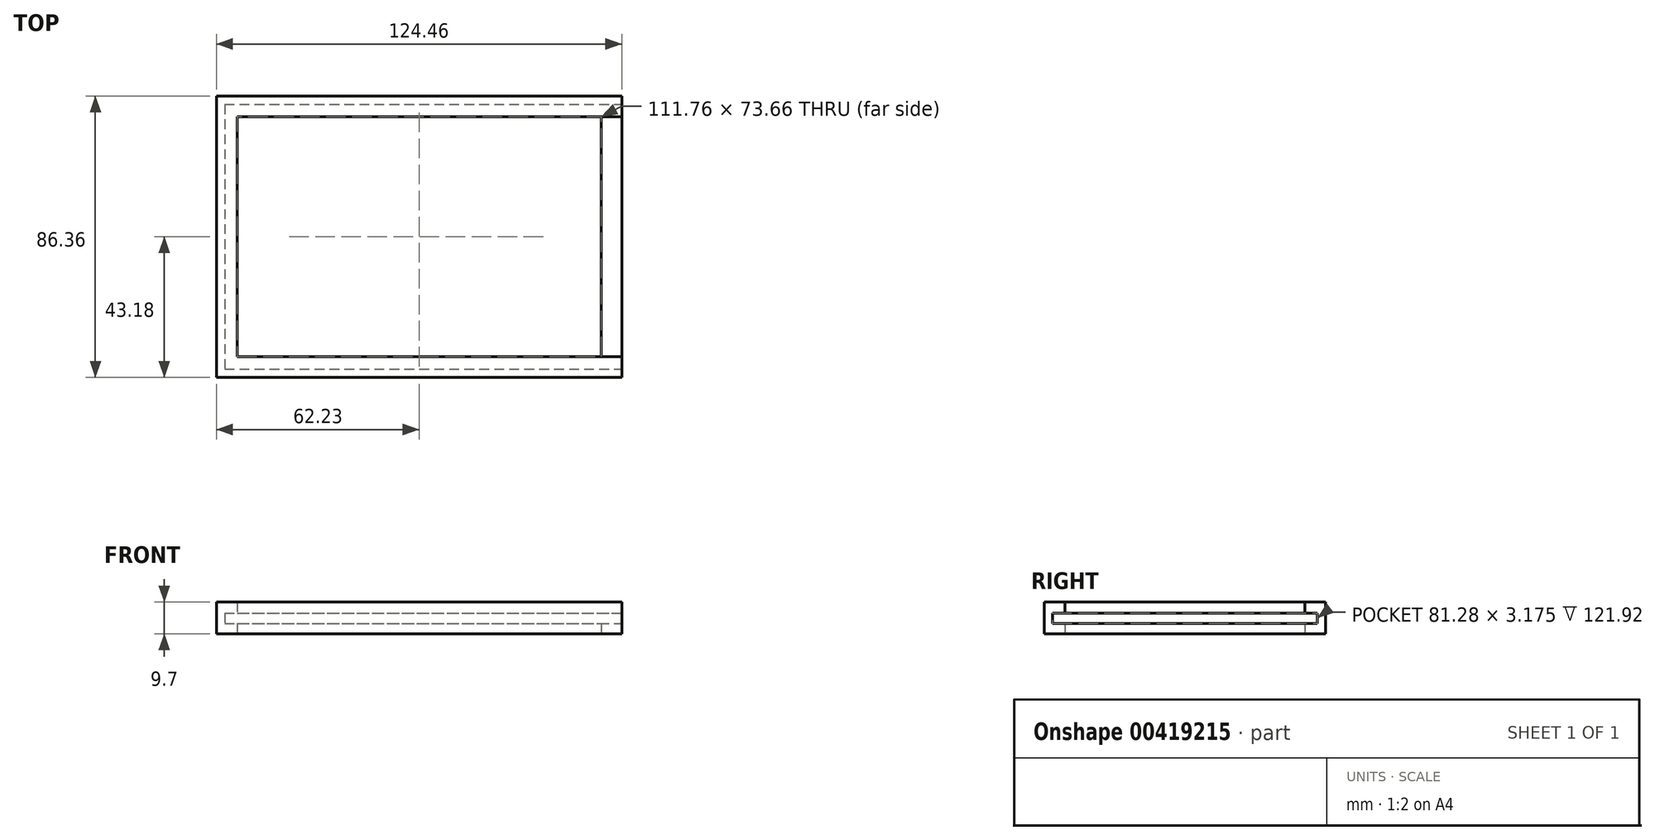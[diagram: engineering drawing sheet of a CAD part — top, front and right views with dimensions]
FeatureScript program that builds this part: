
annotation { "Feature Type Name" : "Feature", "Feature Type Description" : "" }
export const myFeature = defineFeature(function(context is Context, id is Id, definition is map)
    precondition{}
    {
        {
            var Q0;
            Q0=qCreatedBy(makeId("Top.planeOp"),FACE);
            var sketch = newSketch(context, id + "F0", { "sketchPlane" : qUnion([Q0])});
            skLineSegment(sketch, "E0.bottom", {"start": v(-55.88, 36.83) * mm, "end": v(55.88, 36.83) * mm});
            skLineSegment(sketch, "E0.top", {"start": v(-55.88, -36.83) * mm, "end": v(55.88, -36.83) * mm});
            skLineSegment(sketch, "E0.left", {"start": v(-55.88, 36.83) * mm, "end": v(-55.88, -36.83) * mm});
            skLineSegment(sketch, "E0.right", {"start": v(55.88, 36.83) * mm, "end": v(55.88, -36.83) * mm});
            skPoint(sketch, "E0.middle", {"position": v(0, 0) * mm});
            skLineSegment(sketch, "E1.bottom", {"start": v(-59.7, 40.64) * mm, "end": v(59.7, 40.64) * mm});
            skLineSegment(sketch, "E1.top", {"start": v(-59.7, -40.64) * mm, "end": v(59.7, -40.64) * mm});
            skLineSegment(sketch, "E1.left", {"start": v(-59.7, 40.64) * mm, "end": v(-59.7, -40.64) * mm});
            skLineSegment(sketch, "E1.right", {"start": v(59.7, 40.64) * mm, "end": v(59.7, -40.64) * mm});
            skLineSegment(sketch, "E2.bottom", {"start": v(-62.23, 43.18) * mm, "end": v(62.23, 43.18) * mm});
            skLineSegment(sketch, "E2.top", {"start": v(-62.23, -43.18) * mm, "end": v(62.23, -43.18) * mm});
            skLineSegment(sketch, "E2.left", {"start": v(-62.23, 43.18) * mm, "end": v(-62.23, -43.18) * mm});
            skLineSegment(sketch, "E2.right", {"start": v(62.23, 43.18) * mm, "end": v(62.23, -43.18) * mm});
            skLineSegment(sketch, "E3", {"start": v(59.7, 40.64) * mm, "end": v(62.23, 40.64) * mm});
            skLineSegment(sketch, "E4", {"start": v(55.88, 36.83) * mm, "end": v(62.23, 36.83) * mm});
            skLineSegment(sketch, "E5", {"start": v(55.88, -36.83) * mm, "end": v(62.23, -36.83) * mm});
            skLineSegment(sketch, "E6", {"start": v(59.7, -40.64) * mm, "end": v(62.23, -40.64) * mm});
            skSolve(sketch);
        }
        {
            var Q0;
            Q0=makeQuery(id+"F0.imprint","IMPRINT",FACE,{"disambiguationData":[TD([[makeQuery(id+"F0.imprint","IMPRINT",EDGE,{"derivedFrom":sQuery(id+"F0.wireOp",EDGE,"E0.bottom")}),1.0]])]});
            var Q1;
            {var subQ0=sQuery(id+"F0.wireOp",EDGE,"E3");Q1=makeQuery(id+"F0.imprint","IMPRINT",FACE,{"disambiguationData":[TD([[makeQuery(id+"F0.imprint","IMPRINT",EDGE,{"derivedFrom":subQ0}),-1.0]])]});}
            var Q2;
            {var subQ0=sQuery(id+"F0.wireOp",EDGE,"E6");Q2=makeQuery(id+"F0.imprint","IMPRINT",FACE,{"disambiguationData":[TD([[makeQuery(id+"F0.imprint","IMPRINT",EDGE,{"derivedFrom":subQ0}),1.0]])]});}
            var Q3;
            {var subQ0=sQuery(id+"F0.wireOp",EDGE,"E0.right");Q3=makeQuery(id+"F0.imprint","IMPRINT",FACE,{"disambiguationData":[TD([[makeQuery(id+"F0.imprint","IMPRINT",EDGE,{"derivedFrom":subQ0}),1.0]])]});}
            var Q4;
            {var subQ0=sQuery(id+"F0.wireOp",EDGE,"E4");var subQ1=sQuery(id+"F0.wireOp",EDGE,"E1.right");var subQ2=makeQuery(id+"F0.imprint","INTERSECT",VERTEX,{"derivedFrom":[subQ1,subQ0]});Q4=makeQuery(id+"F0.imprint","IMPRINT",FACE,{"disambiguationData":[TD([[makeQuery(id+"F0.imprint","IMPRINT",EDGE,{"disambiguationData":[TD([[subQ2,-1.0]])],"derivedFrom":subQ1}),1.0]])]});}
            extrude(context, id + "F1", {"entities" : qUnion([Q0, Q1, Q2, Q3, Q4]), "depth" : 3.17 * mm});
        }
        {
            var Q0;
            Q0=makeQuery(id+"F0.imprint","IMPRINT",FACE,{"disambiguationData":[TD([[makeQuery(id+"F0.imprint","IMPRINT",EDGE,{"derivedFrom":sQuery(id+"F0.wireOp",EDGE,"E1.bottom")}),1.0]])]});
            extrude(context, id + "F2", {"entities" : qUnion([Q0]), "operationType" : NewBodyOperationType.ADD, "depth" : 9.7 * mm});
        }
        {
            var Q0;
            {var subQ2=sQuery(id+"F0.wireOp",EDGE,"E0.bottom");Q0=makeQuery(id+"F0.imprint","IMPRINT",FACE,{"disambiguationData":[TD([[makeQuery(id+"F0.imprint","IMPRINT",EDGE,{"derivedFrom":subQ2}),1.0]])]});}
            var Q1;
            {var subQ0=sQuery(id+"F0.wireOp",EDGE,"E6");Q1=makeQuery(id+"F0.imprint","IMPRINT",FACE,{"disambiguationData":[TD([[makeQuery(id+"F0.imprint","IMPRINT",EDGE,{"derivedFrom":subQ0}),1.0]])]});}
            var Q2;
            {var subQ0=sQuery(id+"F0.wireOp",EDGE,"E3");Q2=makeQuery(id+"F0.imprint","IMPRINT",FACE,{"disambiguationData":[TD([[makeQuery(id+"F0.imprint","IMPRINT",EDGE,{"derivedFrom":subQ0}),-1.0]])]});}
            extrude(context, id + "F3", {"entities" : qUnion([Q0, Q1, Q2]), "operationType" : NewBodyOperationType.ADD, "depth" : 9.7 * mm, "hasSecondDirection" : true, "secondDirectionOppositeDirection" : true, "secondDirectionDepth" : -6.35 * mm});
        }
    });
